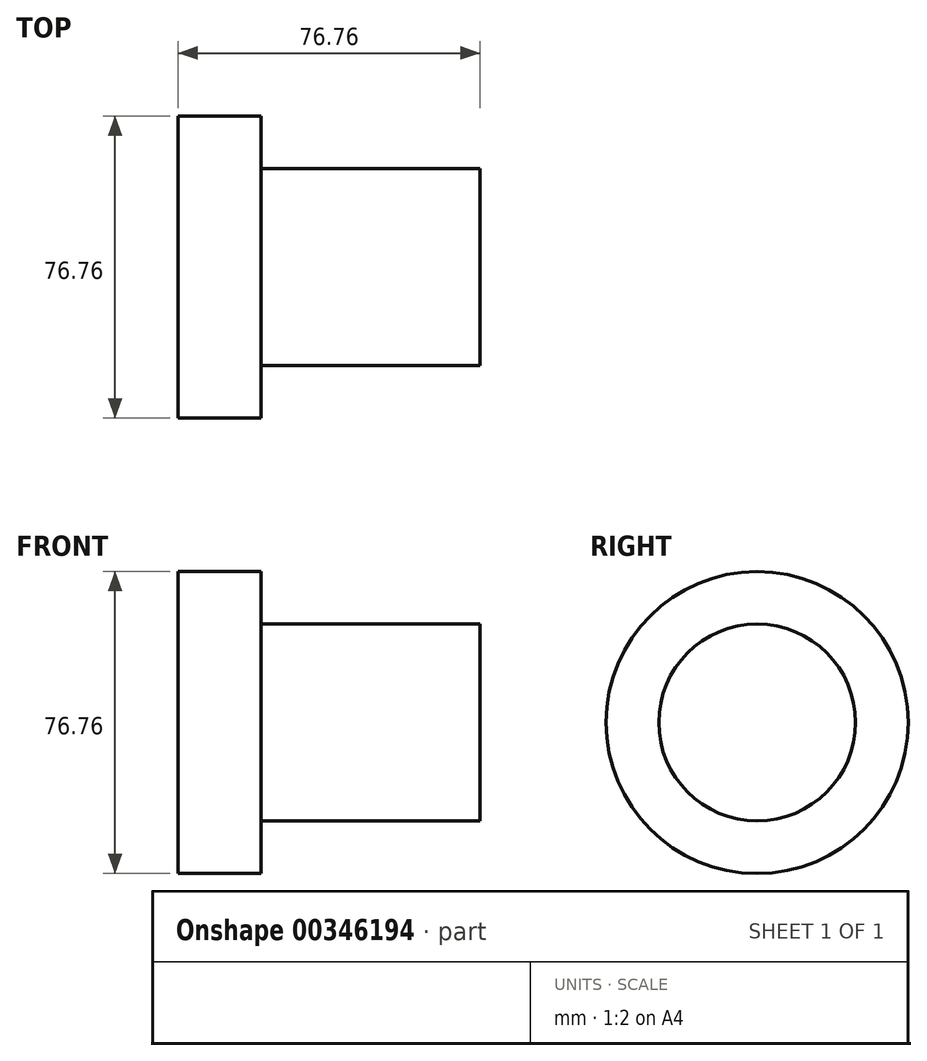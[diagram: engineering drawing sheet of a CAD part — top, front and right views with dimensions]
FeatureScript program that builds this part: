
annotation { "Feature Type Name" : "Feature", "Feature Type Description" : "" }
export const myFeature = defineFeature(function(context is Context, id is Id, definition is map)
    precondition{}
    {
        {
            var Q0;
            Q0=qCreatedBy(makeId("Top.planeOp"),FACE);
            var sketch = newSketch(context, id + "F0", { "sketchPlane" : qUnion([Q0])});
            skLineSegment(sketch, "E0", {"start": v(-60.21, 0) * mm, "end": v(-60.21, 38.38) * mm});
            skLineSegment(sketch, "E1", {"start": v(-60.21, 38.38) * mm, "end": v(-39.08, 38.38) * mm});
            skLineSegment(sketch, "E2", {"start": v(-39.08, 38.38) * mm, "end": v(-39.08, 25) * mm});
            skLineSegment(sketch, "E3", {"start": v(-39.08, 25) * mm, "end": v(16.55, 25) * mm});
            skLineSegment(sketch, "E4", {"start": v(16.55, 25) * mm, "end": v(16.55, 0) * mm});
            skLineSegment(sketch, "E5", {"start": v(16.55, 0) * mm, "end": v(-60.21, 0) * mm});
            skSolve(sketch);
        }
        {
            var Q0;
            Q0=makeQuery(id+"F0.imprint","IMPRINT",FACE,{"disambiguationData":[TD([[makeQuery(id+"F0.imprint","IMPRINT",EDGE,{"derivedFrom":sQuery(id+"F0.wireOp",EDGE,"E0")}),-1.0]])]});
            var Q1;
            Q1=sQuery(id+"F0.wireOp",EDGE,"E5");
            revolve(context, id + "F1", {"entities" : qUnion([Q0]), "axis" : qUnion([Q1]), "revolveType" : RevolveType.FULL});
        }
    });
